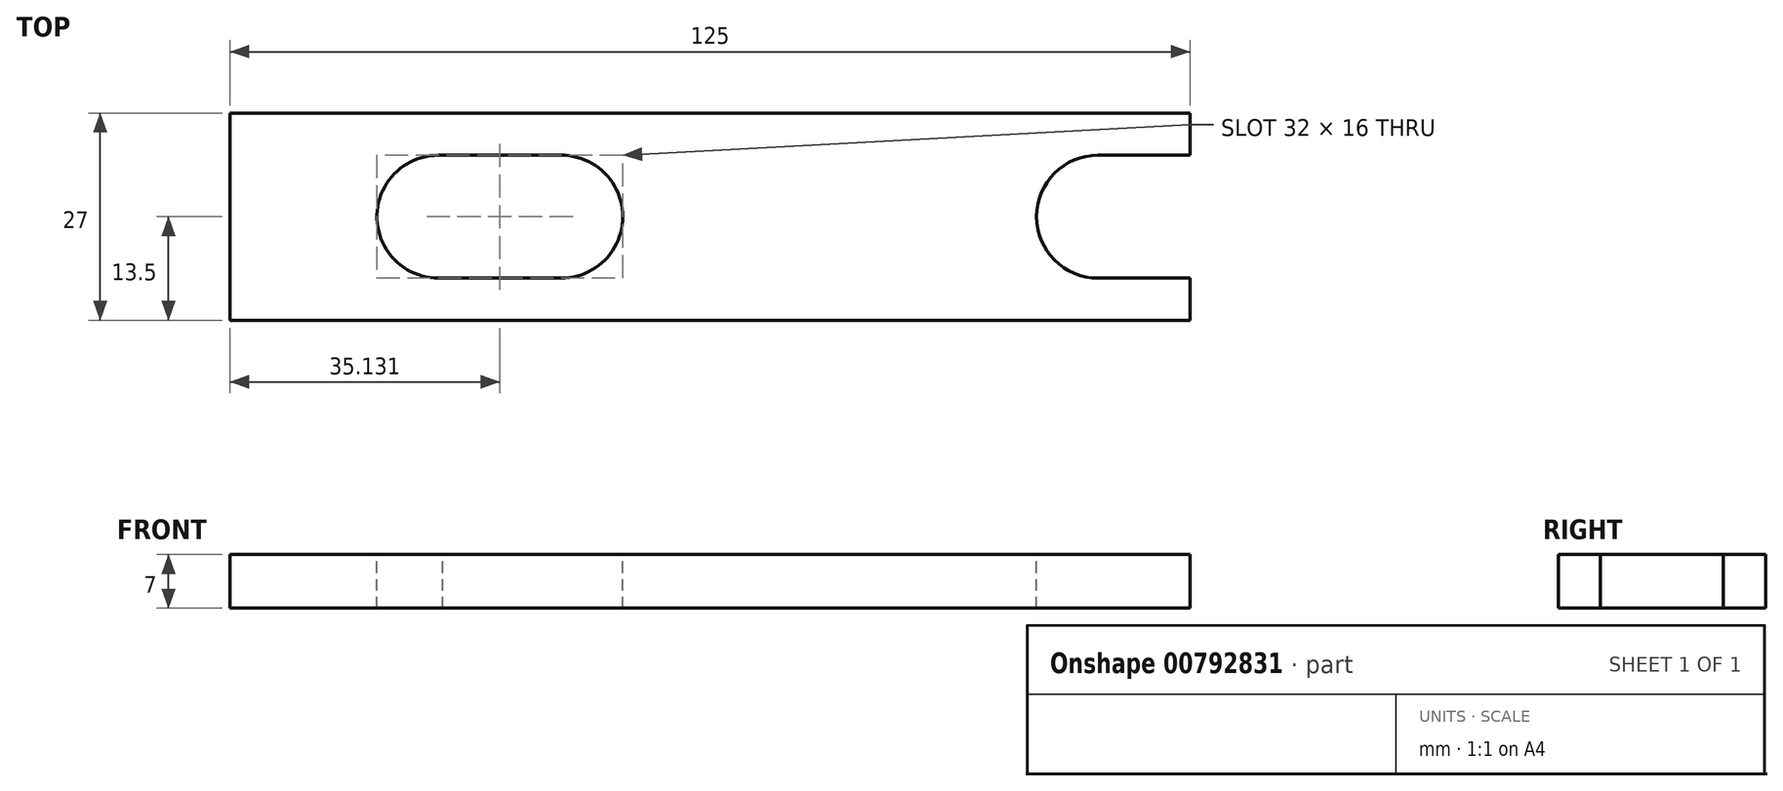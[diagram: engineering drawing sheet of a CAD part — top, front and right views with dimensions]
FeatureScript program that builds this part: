
annotation { "Feature Type Name" : "Feature", "Feature Type Description" : "" }
export const myFeature = defineFeature(function(context is Context, id is Id, definition is map)
    precondition{}
    {
        {
            var Q0;
            Q0=qCreatedBy(makeId("Top.planeOp"),FACE);
            var sketch = newSketch(context, id + "F0", { "sketchPlane" : qUnion([Q0])});
            skLineSegment(sketch, "E0.bottom", {"start": v(125, -13.5) * mm, "end": v(-125, -13.5) * mm});
            skLineSegment(sketch, "E0.top", {"start": v(125, 13.5) * mm, "end": v(-125, 13.5) * mm});
            skLineSegment(sketch, "E0.left", {"start": v(125, -13.5) * mm, "end": v(125, 13.5) * mm});
            skLineSegment(sketch, "E0.right", {"start": v(-125, -13.5) * mm, "end": v(-125, 13.5) * mm});
            skPoint(sketch, "E0.middle", {"position": v(0, 0) * mm});
            skSolve(sketch);
        }
        {
            var Q0;
            Q0 = qSketchRegion(id + "F0", true);
            extrude(context, id + "F1", {"entities" : qUnion([Q0]), "depth" : 7 * mm, "offsetDistance" : 25 * mm});
        }
        {
            var Q0;
            Q0=makeQuery(id+"F1.opExtrude","CAP_FACE",FACE,{"disambiguationData":[OSD([sQuery(id+"F0.wireOp",EDGE,"E0.bottom"),sQuery(id+"F0.wireOp",EDGE,"E0.top"),sQuery(id+"F0.wireOp",EDGE,"E0.left"),sQuery(id+"F0.wireOp",EDGE,"E0.right")])],"isStart":false});
            var sketch = newSketch(context, id + "F2", { "sketchPlane" : qUnion([Q0])});
            skLineSegment(sketch, "E1", {"start": v(-194.56, 0) * mm, "end": v(217.26, 0) * mm, "construction": true});
            skCircle(sketch, "E2", {"center": v(87, 0) * mm, "radius": 8 * mm});
            skCircle(sketch, "E3", {"center": v(71, 0) * mm, "radius": 8 * mm});
            skCircle(sketch, "E4", {"center": v(-12, 0) * mm, "radius": 8 * mm});
            skCircle(sketch, "E5", {"center": v(4, 0) * mm, "radius": 8 * mm});
            skCircle(sketch, "E6", {"center": v(-81.87, 0) * mm, "radius": 8 * mm});
            skCircle(sketch, "E7", {"center": v(-97.87, 0) * mm, "radius": 8 * mm});
            skLineSegment(sketch, "E8", {"start": v(-98.44, -7.98) * mm, "end": v(-81.88, -8) * mm});
            skLineSegment(sketch, "E9", {"start": v(-81.88, -8) * mm, "end": v(-81.88, 8) * mm});
            skLineSegment(sketch, "E10", {"start": v(-81.88, 8) * mm, "end": v(-97.87, 8) * mm});
            skLineSegment(sketch, "E11", {"start": v(-12, 8) * mm, "end": v(4, 8) * mm});
            skLineSegment(sketch, "E12", {"start": v(4, -8) * mm, "end": v(-12, -8) * mm});
            skLineSegment(sketch, "E13", {"start": v(71, -8) * mm, "end": v(87, -8) * mm});
            skLineSegment(sketch, "E14", {"start": v(87, 8) * mm, "end": v(71, 8) * mm});
            skSolve(sketch);
        }
        {
            var Q0;
            Q0 = qSketchRegion(id + "F2", true);
            extrude(context, id + "F3", {"entities" : qUnion([Q0]), "operationType" : NewBodyOperationType.REMOVE, "oppositeDirection" : true, "depth" : 25 * mm, "offsetDistance" : 25 * mm});
        }
        {
            var Q0;
            Q0=makeQuery(id+"F1.opExtrude","CAP_FACE",FACE,{"disambiguationData":[OSD([sQuery(id+"F0.wireOp",EDGE,"E0.bottom"),sQuery(id+"F0.wireOp",EDGE,"E0.top"),sQuery(id+"F0.wireOp",EDGE,"E0.left"),sQuery(id+"F0.wireOp",EDGE,"E0.right")])],"isStart":false});
            var sketch = newSketch(context, id + "F4", { "sketchPlane" : qUnion([Q0])});
            skLineSegment(sketch, "E15", {"start": v(-125, 43.96) * mm, "end": v(-125, -50.87) * mm});
            skLineSegment(sketch, "E16", {"start": v(0, -50.87) * mm, "end": v(0, 43.96) * mm});
            skLineSegment(sketch, "E17", {"start": v(125, 43.96) * mm, "end": v(125, -50.87) * mm});
            skLineSegment(sketch, "E18", {"start": v(125, -50.87) * mm, "end": v(0, -50.87) * mm});
            skLineSegment(sketch, "E19", {"start": v(0, 43.96) * mm, "end": v(125, 43.96) * mm});
            skSolve(sketch);
        }
        {
            var Q0;
            Q0 = qSketchRegion(id + "F4", true);
            extrude(context, id + "F5", {"entities" : qUnion([Q0]), "operationType" : NewBodyOperationType.REMOVE, "oppositeDirection" : true, "depth" : 25 * mm, "offsetDistance" : 25 * mm});
        }
    });
